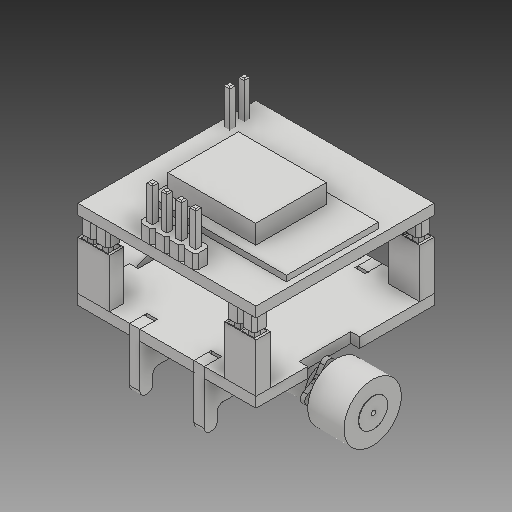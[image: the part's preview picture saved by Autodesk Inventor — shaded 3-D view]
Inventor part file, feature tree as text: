
AUTODESK INVENTOR PART (.ipt)
format: ipt  version: 2017 SP1 (Build 210196100, 196)  size: 986,624 bytes
history: native  units: mm
features: extrude x25, other x20, sketch x16, chamfer x5, fillet x4, projected_geometry x4, pattern_linear x3, mirror x1
ambient origin geometry x8: Origin, YZ Plane, XZ Plane, XY Plane, X Axis, Y Axis, Z Axis, Center Point
bodies: Body1 (feature_tree), Body2 (feature_tree), Body3 (feature_tree), Body4 (feature_tree), Body5 (feature_tree), Body6 (feature_tree), Body7 (feature_tree), Body8 (feature_tree), Body9 (feature_tree), Body10 (feature_tree), Body11 (feature_tree), Body12 (feature_tree), Body13 (feature_tree), Body14 (feature_tree), Body15 (feature_tree)
feature tree (78):
  other  "Bottom_board"
  other  "Bottom_board_plane"
  extrude  "Extrusion1"  Depth=31.0mm
  other  "Charging_frame_R_plane"
  extrude  "Extrusion2"  Depth=1.8mm TaperAngle=0.0deg
  fillet  "Fillet1"  Radius=9.0mm
  extrude  "Extrusion3"  Depth=9.0mm
  fillet  "Fillet2"  Radius=3.0mm
  sketch  "Sketch5"  dims[d11=1.8mm d12=9.0mm]
  extrude  "Extrusion4"  Depth=9.0mm
  fillet  "Fillet3"  [1 undecoded]
  extrude  "Extrusion5"  Depth=2.25mm
  extrude  "Extrusion6"  Depth=3.0mm
  other  "Wheel_R_plane"
  sketch  "Sketch7"  dims[d13=20.0mm d15=28.0mm d16=20.0mm d18=11.2mm d21=-6.5mm]
  extrude  "Extrusion7"  Depth=4.0mm
  extrude  "Extrusion8"  Depth=13.5mm
  mirror  "Mirror1"
  other  "Bottom_board_plane_top"
  sketch  "Sketch8"  dims[d22=10.35mm d23=2.25mm]
  extrude  "Extrusion9"  Depth=31.0mm
  chamfer  "Chamfer1"  Distance=1.8mm
  pattern_linear  "Rectangular Pattern1"  Spacing1=7.5mm  [1 undecoded]
  sketch  "Sketch9"  dims[d24=3.4mm d25=3.0mm]
  extrude  "Extrusion11"  Depth=0.5mm
  extrude  "Extrusion12"  Depth=5.7mm
  chamfer  "Chamfer2"  Distance=1.0mm
  other  "Top_board_plane"
  extrude  "Extrusion13"  TaperAngle=60.0deg  [1 undecoded]
  sketch  "Sketch11"  dims[d30=7.0mm d31=13.5mm]
  extrude  "Extrusion14"  Depth=3.3mm
  extrude  "Extrusion15"  Depth=1.0mm TaperAngle=60.0deg
  chamfer  "Chamfer3"  Distance=0.8mm
  pattern_linear  "Rectangular Pattern2"  Spacing1=0.8mm  [1 undecoded]
  pattern_linear  "Rectangular Pattern3"  Spacing1=0.8mm  [1 undecoded]
  extrude  "Extrusion16"  Depth=2.0mm
  chamfer  "Chamfer4"  Distance=2.0mm
  sketch  "Sketch13"  dims[d34=1.8mm]
  extrude  "Extrusion17"  Depth=1.5mm TaperAngle=0.0deg
  extrude  "Extrusion18"  Depth=0.8mm
  extrude  "Extrusion19"  Depth=6.0mm TaperAngle=0.0deg
  extrude  "Extrusion20"  [1 undecoded]
  other  "Top_board_plane_top"
  sketch  "Sketch14"  dims[d35=1.6mm d36=1.8mm d37=0.0mm]
  extrude  "Extrusion21"  Depth=10.0mm
  extrude  "Extrusion22"  Depth=6.3mm TaperAngle=0.0deg
  chamfer  "Chamfer5"  Distance=5.0mm
  sketch  "Sketch17"  dims[d39=0.5mm]
  extrude  "Extrusion25"  Depth=0.1mm TaperAngle=0.0deg
  fillet  "Fillet4"  Radius=1.8mm
  extrude  "Extrusion26"  Depth=2.5mm
  sketch  "Sketch15"  dims[d38=1.0mm]
  extrude  "Extrusion23"  Depth=5.5mm
  extrude  "Extrusion24"  Depth=8.5mm TaperAngle=0.0deg
  sketch  "Sketch2"  dims[d2=4.5mm d3=31.0mm]
  sketch  "Sketch3"  dims[d4=31.0mm d5=1.8mm d6=0.0mm d7=9.0mm]
  other  "Charging_frame_R"
  sketch  "Sketch4"  dims[d8=1.5mm d9=9.0mm d10=3.0mm]
  other  "Motor_R"
  projected_geometry  "Projected Loop2"
  other  "Wheel_R"
  other  "Bottom_board_connectors"
  other  "Pattern of Charging_frame_R:1"
  other  "Charging_frame_L"
  other  "Pattern of Motor_R:2"
  other  "Motor_L"
  other  "Pattern of Wheel_R:3"
  other  "Wheel_L"
  sketch  "Sketch10"  dims[d26=2.5mm d27=4.0mm]
  other  "Top_board"
  other  "Top_board_connectors"
  sketch  "Sketch12"  dims[d32=1.8mm d33=31.0mm]
  projected_geometry  "Projected Loop3"
  other  "WiFi_board"
  sketch  "Sketch18"  dims[d40=13.5mm]
  projected_geometry  "Projected Loop4"
  sketch  "Sketch19"  dims[d41=6.0mm d42=7.5mm d43=0.0mm d44=0.5mm d45=5.7mm d46=1.0mm d47=60.0deg d48=3.3mm d49=1.0mm d50=60.0deg d51=3.3mm d52=0.8mm d53=0.8mm d54=0.8mm d55=0.0mm d56=2.0mm d57=2.0mm d58=1.5mm d59=0.0mm d60=0.8mm d61=6.0mm d62=0.0mm d63=-16.0mm d64=10.0mm d65=6.3mm d66=0.0mm d67=5.0mm d68=0.1mm d69=6.4mm d70=0.0mm d71=0.0mm d72=1.8mm d73=2.5mm d74=5.5mm d75=8.5mm d76=0.0mm d77=1.0mm d78=1.5mm d81=0.6mm d82=2.0mm d83=45.0deg d84=20.0mm d86=25.5mm d87=20.0mm d89=28.5mm d90=2.5mm d91=2.5mm d92=0.5mm d93=0.5mm d94=0.5mm d95=0.5mm d96=0.5mm d97=0.5mm d98=0.5mm d99=20.0mm d101=2.5mm d102=10.0mm d104=10.0mm d106=20.0mm d108=2.5mm d109=10.0mm d111=10.0mm d113=2.5mm d114=0.0mm d115=1.0mm d116=30.0mm d118=2.5mm d119=10.0mm d121=10.0mm d123=8.2mm d124=0.0mm d125=0.2mm d126=2.0mm d127=45.0deg d128=13.6mm d129=1.8mm d130=0.0mm d131=1.0mm d132=1.0mm d133=0.75mm d134=2.5mm d135=0.5mm d136=0.5mm d137=0.5mm d138=0.5mm d139=0.5mm d140=0.5mm d141=0.5mm d142=0.5mm d143=20.0mm d145=2.5mm d146=10.0mm d148=10.0mm d150=2.5mm d151=0.0mm d152=8.2mm d153=0.0mm d154=0.2mm d155=2.0mm d156=45.0deg d157=20.0mm d159=28.5mm d160=20.0mm d162=25.5mm d163=2.5mm d164=8.1mm d165=8.5mm d166=0.0mm d167=0.6mm d168=2.0mm d169=45.0deg d170=8.5mm d171=11.2mm d172=1.8mm d173=0.0mm d176=1.5mm d177=1.25mm d178=1.7mm d186=1.8mm d187=0.0mm d188=1.0mm d189=20.0mm d191=2.5mm d192=10.0mm d194=10.0mm d196=8.5mm d197=0.0mm d198=0.2mm d199=2.0mm d200=45.0deg d201=30.0mm d203=2.5mm d204=10.0mm d206=10.0mm d208=8.2mm d209=0.0mm d210=2.6mm d211=0.0mm d212=1.8mm d213=2.5mm d214=2.5mm d215=2.5mm d216=0.5mm d217=0.5mm d218=0.5mm d219=0.5mm d220=0.5mm d221=0.5mm d222=0.5mm d223=0.5mm d224=1.0mm d225=1.0mm d226=40.0mm d228=2.5mm d229=10.0mm d231=10.0mm d233=2.5mm d234=0.0mm d235=8.5mm d236=0.0mm d237=16.0mm d238=24.0mm d240=1.0mm d241=22.3mm d242=12.3mm d243=15.3mm d244=1.5mm d245=1.0mm d246=0.0mm d247=4.3mm d248=0.0mm d251=6.63mm d252=2.8mm d253=17.7mm d254=1.35mm d255=0.0mm d256=0.5mm d257=0.7mm d258=0.0mm]
  projected_geometry  "Projected Loop5"
note: 6 required parameter values undecoded (feature->parameter linkage not recoverable at this tier; creation-order binding heuristic only, values carry confidence <= 0.55)
